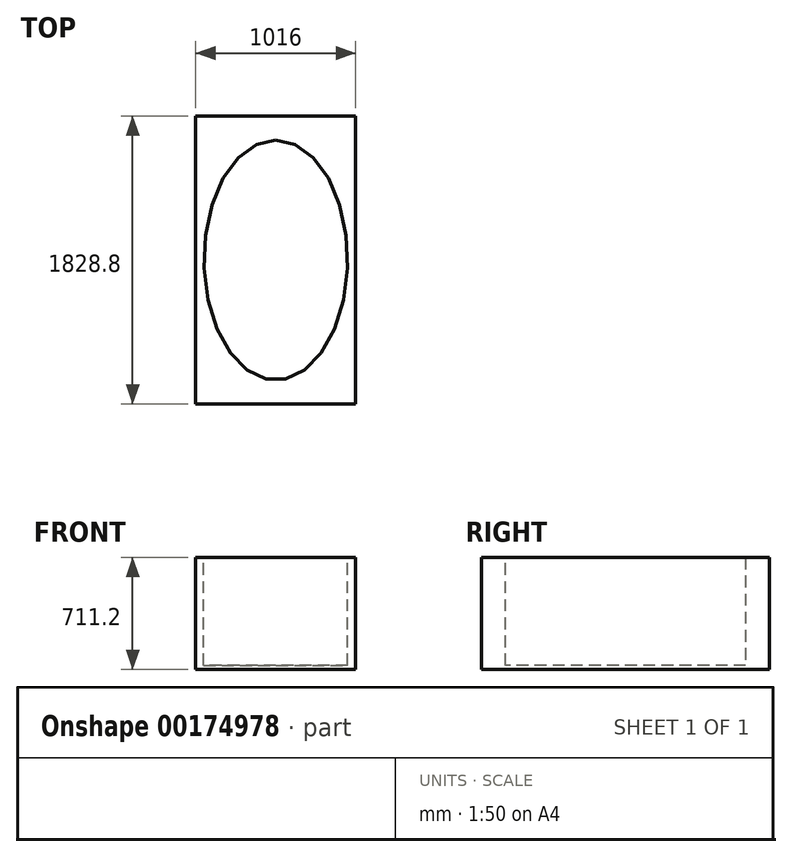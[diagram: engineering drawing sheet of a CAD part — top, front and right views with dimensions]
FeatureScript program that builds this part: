
annotation { "Feature Type Name" : "Feature", "Feature Type Description" : "" }
export const myFeature = defineFeature(function(context is Context, id is Id, definition is map)
    precondition{}
    {
        {
            var Q0;
            Q0=qCreatedBy(makeId("Top.planeOp"),FACE);
            var sketch = newSketch(context, id + "F0", { "sketchPlane" : qUnion([Q0])});
            skLineSegment(sketch, "E0", {"start": v(0, 0) * mm, "end": v(1016, 0) * mm});
            skLineSegment(sketch, "E1", {"start": v(1016, 0) * mm, "end": v(1016, 1828.8) * mm});
            skLineSegment(sketch, "E2", {"start": v(1016, 1828.8) * mm, "end": v(0, 1828.8) * mm});
            skLineSegment(sketch, "E3", {"start": v(0, 1828.8) * mm, "end": v(0, 0) * mm});
            skEllipse(sketch, "E4", {"center": v(508, 914.4) * mm, "majorRadius": 762 * mm, "minorRadius": 457.2 * mm, "majorAxis": v(0, 1)});
            skPoint(sketch, "E4.centerSnap0", {"position": v(508, 1828.8) * mm});
            skPoint(sketch, "E4.centerSnap1", {"position": v(0, 914.4) * mm});
            skSolve(sketch);
        }
        {
            var Q0;
            Q0=makeQuery(id+"F0.imprint","IMPRINT",FACE,{"disambiguationData":[TD([[makeQuery(id+"F0.imprint","IMPRINT",EDGE,{"derivedFrom":sQuery(id+"F0.wireOp",EDGE,"E0")}),1.0]])]});
            extrude(context, id + "F1", {"entities" : qUnion([Q0]), "depth" : 711.2 * mm});
        }
        {
            var Q0;
            Q0=makeQuery(id+"F0.imprint","IMPRINT",FACE,{"disambiguationData":[TD([[makeQuery(id+"F0.imprint","IMPRINT",EDGE,{"derivedFrom":sQuery(id+"F0.wireOp",EDGE,"E4")}),1.0]])]});
            extrude(context, id + "F2", {"entities" : qUnion([Q0]), "operationType" : NewBodyOperationType.ADD, "depth" : 25.4 * mm});
        }
    });
